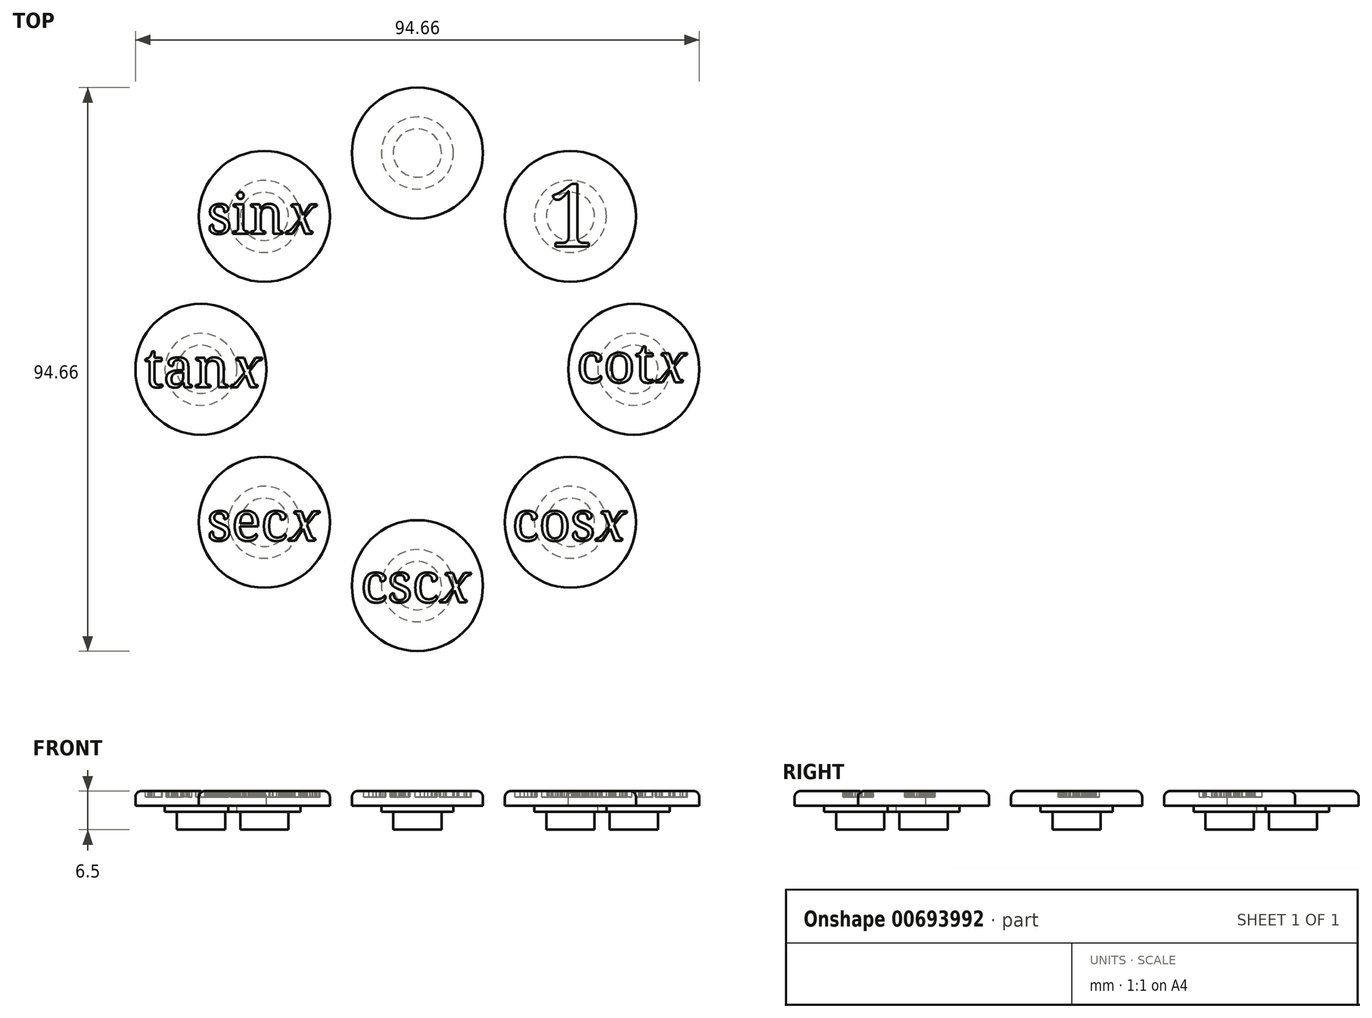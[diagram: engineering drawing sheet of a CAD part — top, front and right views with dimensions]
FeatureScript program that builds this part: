
annotation { "Feature Type Name" : "Feature", "Feature Type Description" : "" }
export const myFeature = defineFeature(function(context is Context, id is Id, definition is map)
    precondition{}
    {
        {
            var Q0;
            Q0=qCreatedBy(makeId("Top.planeOp"),FACE);
            var sketch = newSketch(context, id + "F0", { "sketchPlane" : qUnion([Q0])});
            skCircle(sketch, "E0", {"center": v(0, 0) * mm, "radius": 11 * mm});
            skCircle(sketch, "E1.0", {"center": v(0, 0) * mm, "radius": 4.05 * mm});
            skCircle(sketch, "E2.0", {"center": v(0, 0) * mm, "radius": 6.05 * mm});
            skSolve(sketch);
        }
        {
            var Q0;
            Q0=makeQuery(id+"F0.imprint","IMPRINT",FACE,{"disambiguationData":[TD([[makeQuery(id+"F0.imprint","IMPRINT",EDGE,{"derivedFrom":sQuery(id+"F0.wireOp",EDGE,"E0")}),1.0]])]});
            extrude(context, id + "F1", {"entities" : qUnion([Q0]), "depth" : 2.5 * mm, "offsetDistance" : 25.4 * mm});
        }
        {
            var Q0;
            Q0=makeQuery(id+"F0.imprint","IMPRINT",FACE,{"disambiguationData":[TD([[makeQuery(id+"F0.imprint","IMPRINT",EDGE,{"derivedFrom":sQuery(id+"F0.wireOp",EDGE,"E1.0")}),1.0]])]});
            var Q1;
            Q1=makeQuery(id+"F0.imprint","IMPRINT",FACE,{"disambiguationData":[TD([[makeQuery(id+"F0.imprint","IMPRINT",EDGE,{"derivedFrom":sQuery(id+"F0.wireOp",EDGE,"E1.0")}),-1.0]])]});
            extrude(context, id + "F2", {"entities" : qUnion([Q0, Q1]), "operationType" : NewBodyOperationType.ADD, "depth" : 3.5 * mm, "offsetDistance" : 25.4 * mm});
        }
        {
            var Q0;
            Q0=makeQuery(id+"F0.imprint","IMPRINT",FACE,{"disambiguationData":[TD([[makeQuery(id+"F0.imprint","IMPRINT",EDGE,{"derivedFrom":sQuery(id+"F0.wireOp",EDGE,"E1.0")}),1.0]])]});
            extrude(context, id + "F3", {"entities" : qUnion([Q0]), "operationType" : NewBodyOperationType.ADD, "depth" : 6.5 * mm, "offsetDistance" : 25.4 * mm});
        }
        {
            var Q0;
            Q0=makeQuery(id+"F1.opExtrude","CAP_EDGE",EDGE,{"disambiguationData":[OSD([sQuery(id+"F0.wireOp",EDGE,"E0")])],"isStart":true});
            fillet(context, id + "F4", {"entities" : qUnion([Q0]), "radius" : 1.02 * mm, "tangentPropagation" : true, "allowEdgeOverflow" : false});
        }
        {
            var Q0;
            Q0=qCreatedBy(makeId("Right.planeOp"),FACE);
            var sketch = newSketch(context, id + "F5", { "sketchPlane" : qUnion([Q0])});
            skLineSegment(sketch, "E3", {"start": v(-36.33, -6.15) * mm, "end": v(-36.33, 36.38) * mm});
            skLineSegment(sketch, "E4", {"start": v(0, 0) * mm, "end": v(-88.4, 0) * mm});
            skSolve(sketch);
        }
        {
            var Q0;
            Q0=makeQuery(id+"F1.opExtrude","SWEPT_BODY",BODY,{"disambiguationData":[OSD([sQuery(id+"F0.wireOp",EDGE,"E0"),sQuery(id+"F0.wireOp",EDGE,"E2.0")])]});
            var Q1;
            Q1=sQuery(id+"F5.wireOp",EDGE,"E3");
            circularPattern(context, id + "F6", {"entities" : qUnion([Q0]), "axis" : qUnion([Q1]), "angle" : 360 * degree, "instanceCount" : 8, "equalSpace" : true});
        }
        {
            var Q0;
            Q0=makeQuery(id+"F6.opPattern","COPY",BODY,{"derivedFrom":makeQuery(id+"F1.opExtrude","SWEPT_BODY",BODY,{"disambiguationData":[OSD([sQuery(id+"F0.wireOp",EDGE,"E0"),sQuery(id+"F0.wireOp",EDGE,"E2.0")])]}),"instanceName":"7"});
            var Q1;
            Q1=makeQuery(id+"F1.opExtrude","SWEPT_BODY",BODY,{"disambiguationData":[OSD([sQuery(id+"F0.wireOp",EDGE,"E0"),sQuery(id+"F0.wireOp",EDGE,"E2.0")])]});
            var Q2;
            Q2=makeQuery(id+"F6.opPattern","COPY",BODY,{"derivedFrom":makeQuery(id+"F1.opExtrude","SWEPT_BODY",BODY,{"disambiguationData":[OSD([sQuery(id+"F0.wireOp",EDGE,"E0"),sQuery(id+"F0.wireOp",EDGE,"E2.0")])]}),"instanceName":"1"});
            var Q3;
            Q3=makeQuery(id+"F6.opPattern","COPY",BODY,{"derivedFrom":makeQuery(id+"F1.opExtrude","SWEPT_BODY",BODY,{"disambiguationData":[OSD([sQuery(id+"F0.wireOp",EDGE,"E0"),sQuery(id+"F0.wireOp",EDGE,"E2.0")])]}),"instanceName":"2"});
            var Q4;
            Q4=makeQuery(id+"F6.opPattern","COPY",BODY,{"derivedFrom":makeQuery(id+"F1.opExtrude","SWEPT_BODY",BODY,{"disambiguationData":[OSD([sQuery(id+"F0.wireOp",EDGE,"E0"),sQuery(id+"F0.wireOp",EDGE,"E2.0")])]}),"instanceName":"3"});
            var Q5;
            Q5=makeQuery(id+"F6.opPattern","COPY",BODY,{"derivedFrom":makeQuery(id+"F1.opExtrude","SWEPT_BODY",BODY,{"disambiguationData":[OSD([sQuery(id+"F0.wireOp",EDGE,"E0"),sQuery(id+"F0.wireOp",EDGE,"E2.0")])]}),"instanceName":"4"});
            var Q6;
            Q6=makeQuery(id+"F6.opPattern","COPY",BODY,{"derivedFrom":makeQuery(id+"F1.opExtrude","SWEPT_BODY",BODY,{"disambiguationData":[OSD([sQuery(id+"F0.wireOp",EDGE,"E0"),sQuery(id+"F0.wireOp",EDGE,"E2.0")])]}),"instanceName":"5"});
            var Q7;
            Q7=makeQuery(id+"F6.opPattern","COPY",BODY,{"derivedFrom":makeQuery(id+"F1.opExtrude","SWEPT_BODY",BODY,{"disambiguationData":[OSD([sQuery(id+"F0.wireOp",EDGE,"E0"),sQuery(id+"F0.wireOp",EDGE,"E2.0")])]}),"instanceName":"6"});
            var Q8;
            Q8=sQuery(id+"F5.wireOp",EDGE,"E4");
            transform(context, id + "F7", {"entities" : qUnion([Q0, Q1, Q2, Q3, Q4, Q5, Q6, Q7]), "transformType" : TransformType.ROTATION, "transformAxis" : qUnion([Q8]), "angle" : 180 * degree, "makeCopy" : false});
        }
        {
            var Q0;
            Q0=qCreatedBy(makeId("Top.planeOp"),FACE);
            var sketch = newSketch(context, id + "F8", { "sketchPlane" : qUnion([Q0])});
            skText(sketch, "E5", { "text": "sin", "fontName": "NotoSerif-Regular.ttf"});
            skText(sketch, "E6", { "text": "x", "fontName": "NotoSerif-Italic.ttf"});
            skText(sketch, "E7", { "text": "tan", "fontName": "NotoSerif-Regular.ttf"});
            skText(sketch, "E8", { "text": "x", "fontName": "NotoSerif-Italic.ttf"});
            skText(sketch, "E9", { "text": "sec", "fontName": "NotoSerif-Regular.ttf"});
            skText(sketch, "E10", { "text": "x", "fontName": "NotoSerif-Italic.ttf"});
            skText(sketch, "E11", { "text": "csc", "fontName": "NotoSerif-Regular.ttf"});
            skText(sketch, "E12", { "text": "x", "fontName": "NotoSerif-Italic.ttf"});
            skText(sketch, "E13", { "text": "cos", "fontName": "NotoSerif-Regular.ttf"});
            skText(sketch, "E14", { "text": "x", "fontName": "NotoSerif-Italic.ttf"});
            skText(sketch, "E15", { "text": "cot", "fontName": "NotoSerif-Regular.ttf"});
            skText(sketch, "E16", { "text": "x", "fontName": "NotoSerif-Italic.ttf"});
            skText(sketch, "E17", { "text": "1", "fontName": "NotoSerif-Regular.ttf"});
            const initialGuessF8  = {"E5": [-0.0353, -0.01354, 1, 0, 0.0066], "E6": [-0.02196, -0.01354, 1, 0, 0.0066], "E7": [-0.04584, -0.03933, 1, 0, 0.0066], "E8": [-0.03119, -0.03933, 1, 0, 0.0066], "E9": [-0.0353, -0.0651, 1, 0, 0.0066], "E10": [-0.0215, -0.0651, 1, 0, 0.0066], "E11": [-0.0095, -0.07545, 1, 0, 0.0066], "E12": [0.0039, -0.07545, 1, 0, 0.0066], "E13": [0.01591, -0.0651, 1, 0, 0.0066], "E14": [0.03005, -0.0651, 1, 0, 0.0066], "E15": [0.02674, -0.03853, 1, 0, 0.0066], "E16": [0.04016, -0.03853, 1, 0, 0.0066], "E17": [0.0218, -0.01572, 1, 0, 0.01055]};
            skSetInitialGuess(sketch, initialGuessF8);
            skSolve(sketch);
        }
        {
            var Q0;
            Q0 = qSketchRegion(id + "F8", true);
            extrude(context, id + "F9", {"entities" : qUnion([Q0]), "operationType" : NewBodyOperationType.REMOVE, "oppositeDirection" : true, "depth" : 1 * mm, "offsetDistance" : 25 * mm});
        }
    });
